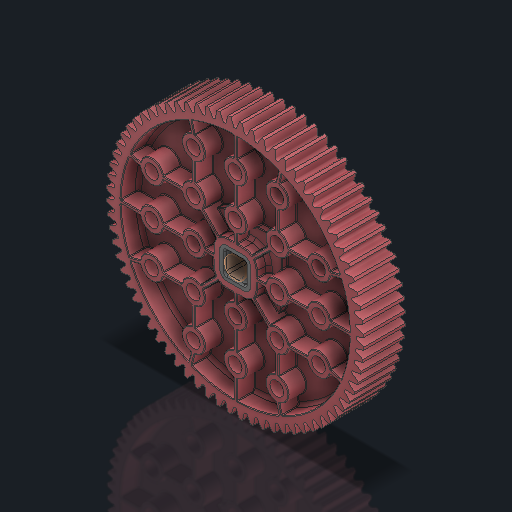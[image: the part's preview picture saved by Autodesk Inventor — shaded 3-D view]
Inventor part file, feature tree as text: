
AUTODESK INVENTOR PART (.ipt)
format: ipt  version: 2023.2 (Build 272271030, 271C)  size: 6,645,760 bytes
history: native  units: in
note: dims shown in document units (in); Inventor stores cm internally (conversion verified against a paired STEP export)
features: other x6, sketch x1
ambient origin geometry x8: Origin, YZ Plane, XZ Plane, XY Plane, X Axis, Y Axis, Z Axis, Center Point
bodies: Solid1 (feature_tree), Solid2 (feature_tree)
feature tree (7):
  other  "HS 72T Gear, No Insert.ipt"
  other  "Solid1::HS 72T Gear, No Insert.ipt"
  other  "Solid2::HS 72T Gear, No Insert.ipt"
  other  "TaggingFeature1"
  sketch  "Sketch1"  dims[d0=0.3937in]
  other  "Srf1"
  other  "Srf1::Derived"
